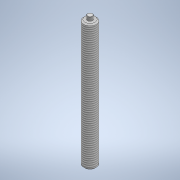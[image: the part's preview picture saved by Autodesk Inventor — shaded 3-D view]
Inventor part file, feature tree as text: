
AUTODESK INVENTOR PART (.ipt)
format: ipt  version: 2020 (Build 240168000, 168)  size: 114,176 bytes
history: native  units: mm
features: extrude x2, chamfer x2, thread x2, sketch x2, other x1
ambient origin geometry x8: Origin, YZ Plane, XZ Plane, XY Plane, X Axis, Y Axis, Z Axis, Center Point
bodies: Body1 (feature_tree)
feature tree (9):
  other  "Твердое тело1"
  extrude  "Выдавливание1"  Depth=10.0mm
  chamfer  "Фаска1"  Distance=100.0mm
  thread  "Резьба1"
  extrude  "Выдавливание2"  Depth=2.0mm TaperAngle=45.0deg
  chamfer  "Фаска2"  Distance=98.0mm
  thread  "Резьба2"
  sketch  "Эскиз1"
  sketch  "Эскиз2"
